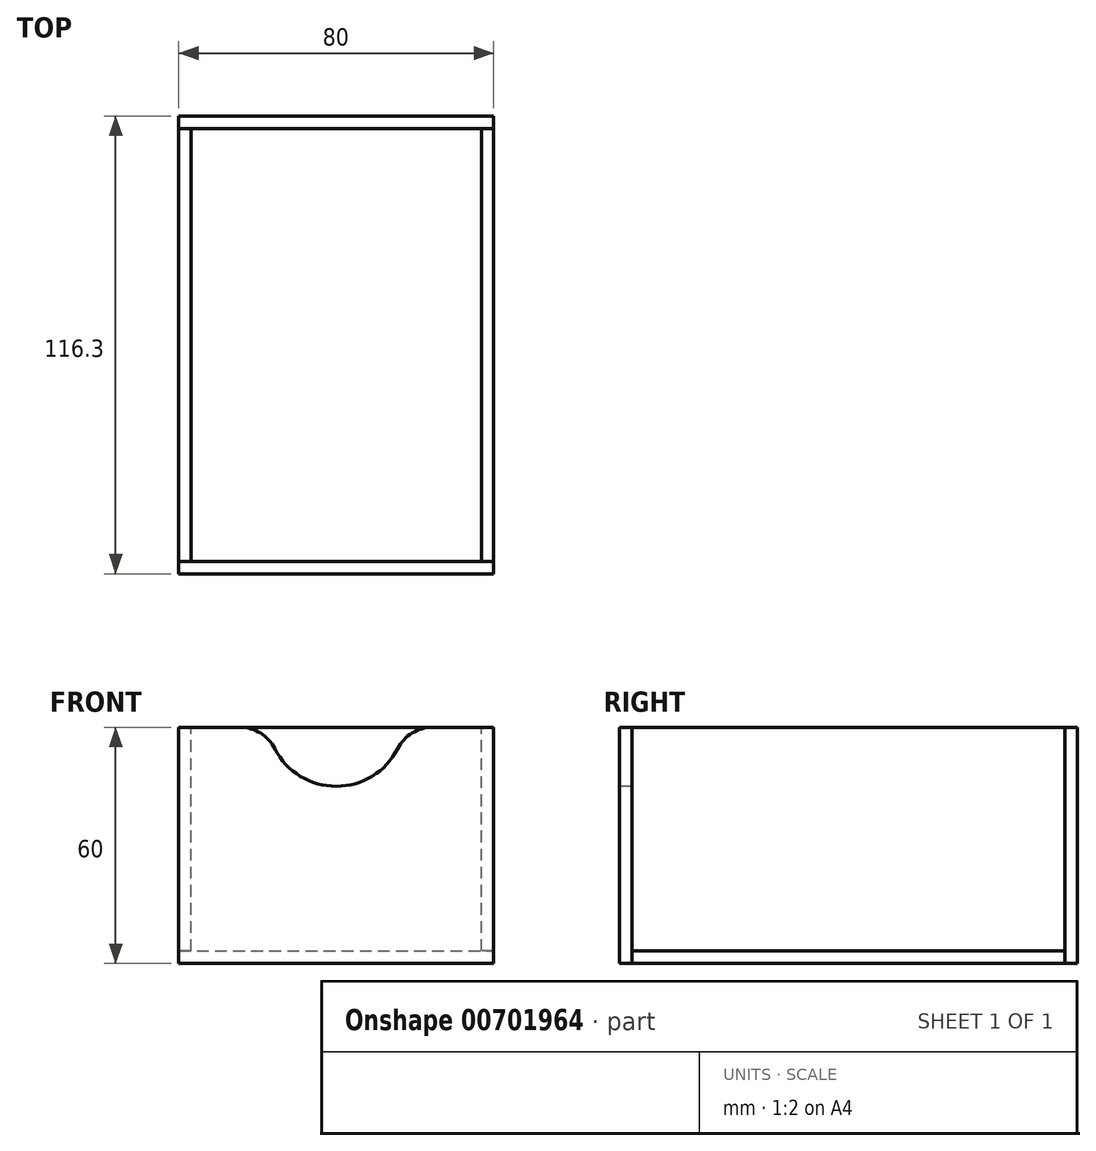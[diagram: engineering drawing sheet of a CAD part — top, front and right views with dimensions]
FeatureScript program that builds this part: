
annotation { "Feature Type Name" : "Feature", "Feature Type Description" : "" }
export const myFeature = defineFeature(function(context is Context, id is Id, definition is map)
    precondition{}
    {
        {
            var Q0;
            Q0=qCreatedBy(makeId("Front.planeOp"),FACE);
            var sketch = newSketch(context, id + "F0", { "sketchPlane" : qUnion([Q0])});
            skLineSegment(sketch, "E0.bottom", {"start": v(0, 0) * mm, "end": v(80, 0) * mm});
            skLineSegment(sketch, "E0.top", {"start": v(0, 60) * mm, "end": v(80, 60) * mm});
            skLineSegment(sketch, "E0.left", {"start": v(0, 0) * mm, "end": v(0, 60) * mm});
            skLineSegment(sketch, "E0.right", {"start": v(80, 0) * mm, "end": v(80, 60) * mm});
            skSolve(sketch);
        }
        {
            var Q0;
            Q0=qSketchRegion(id+"F0",true);
            extrude(context, id + "F1", {"entities" : qUnion([Q0]), "depth" : 3.15 * mm, "offsetDistance" : 25 * mm});
        }
        {
            var Q0;
            Q0=makeQuery(id+"F1.opExtrude","SWEPT_FACE",FACE,{"disambiguationData":[OSD([sQuery(id+"F0.wireOp",EDGE,"E0.bottom")])]});
            var sketch = newSketch(context, id + "F2", { "sketchPlane" : qUnion([Q0])});
            skLineSegment(sketch, "E1.bottom", {"start": v(0, 0) * mm, "end": v(80, 0) * mm});
            skLineSegment(sketch, "E1.top", {"start": v(0, -110) * mm, "end": v(80, -110) * mm});
            skLineSegment(sketch, "E1.left", {"start": v(0, 0) * mm, "end": v(0, -110) * mm});
            skLineSegment(sketch, "E1.right", {"start": v(80, 0) * mm, "end": v(80, -110) * mm});
            skSolve(sketch);
        }
        {
            var Q0;
            Q0=qSketchRegion(id+"F2",true);
            extrude(context, id + "F3", {"entities" : qUnion([Q0]), "oppositeDirection" : true, "depth" : 3.15 * mm, "offsetDistance" : 25 * mm});
        }
        {
            var Q0;
            Q0=makeQuery(id+"F3.opExtrude","SWEPT_FACE",FACE,{"disambiguationData":[OSD([sQuery(id+"F2.wireOp",EDGE,"E1.left")])]});
            var sketch = newSketch(context, id + "F4", { "sketchPlane" : qUnion([Q0])});
            skLineSegment(sketch, "E2.bottom", {"start": v(-110, 3.15) * mm, "end": v(0, 3.15) * mm});
            skLineSegment(sketch, "E2.top", {"start": v(-110, 60) * mm, "end": v(0, 60) * mm});
            skLineSegment(sketch, "E2.left", {"start": v(-110, 3.15) * mm, "end": v(-110, 60) * mm});
            skLineSegment(sketch, "E2.right", {"start": v(0, 3.15) * mm, "end": v(0, 60) * mm});
            skSolve(sketch);
        }
        {
            var Q0;
            Q0=qSketchRegion(id+"F4",true);
            extrude(context, id + "F5", {"entities" : qUnion([Q0]), "oppositeDirection" : true, "depth" : 3.15 * mm, "offsetDistance" : 25 * mm});
        }
        {
            var Q0;
            Q0=makeQuery(id+"F5.opExtrude","SWEPT_BODY",BODY,{"disambiguationData":[OSD([sQuery(id+"F4.wireOp",EDGE,"E2.bottom"),sQuery(id+"F4.wireOp",EDGE,"E2.top"),sQuery(id+"F4.wireOp",EDGE,"E2.left"),sQuery(id+"F4.wireOp",EDGE,"E2.right")])]});
            transform(context, id + "F6", {"entities" : qUnion([Q0]), "transformType" : TransformType.TRANSLATION_3D, "dx" : (81.85 - 5) * mm, "dy" : 0 * mm, "dz" : 0 * mm, "makeCopy" : true});
        }
        {
            var Q0;
            Q0=makeQuery(id+"F3.opExtrude","SWEPT_FACE",FACE,{"disambiguationData":[OSD([sQuery(id+"F2.wireOp",EDGE,"E1.top")])]});
            var sketch = newSketch(context, id + "F7", { "sketchPlane" : qUnion([Q0])});
            skLineSegment(sketch, "E3.bottom", {"start": v(-80, 0) * mm, "end": v(0, 0) * mm});
            skLineSegment(sketch, "E3.top", {"start": v(-80, 60) * mm, "end": v(0, 60) * mm});
            skLineSegment(sketch, "E3.left", {"start": v(-80, 0) * mm, "end": v(-80, 60) * mm});
            skLineSegment(sketch, "E3.right", {"start": v(0, 0) * mm, "end": v(0, 60) * mm});
            skSolve(sketch);
        }
        {
            var Q0;
            Q0=qSketchRegion(id+"F7",true);
            extrude(context, id + "F8", {"entities" : qUnion([Q0]), "depth" : 3.15 * mm, "offsetDistance" : 25 * mm});
        }
        {
            var Q0;
            Q0=makeQuery(id+"F1.opExtrude","CAP_FACE",FACE,{"disambiguationData":[OSD([sQuery(id+"F0.wireOp",EDGE,"E0.bottom"),sQuery(id+"F0.wireOp",EDGE,"E0.top"),sQuery(id+"F0.wireOp",EDGE,"E0.left"),sQuery(id+"F0.wireOp",EDGE,"E0.right")])],"isStart":false});
            var sketch = newSketch(context, id + "F9", { "sketchPlane" : qUnion([Q0])});
            skCircle(sketch, "E4", {"center": v(40, 62.5) * mm, "radius": 17.5 * mm});
            skPoint(sketch, "E4.centerSnap0", {"position": v(40, 60) * mm});
            skLineSegment(sketch, "E5", {"start": v(40, 60) * mm, "end": v(40, 62.5) * mm, "construction": true});
            skSolve(sketch);
        }
        {
            var Q0;
            Q0=qSketchRegion(id+"F9",true);
            extrude(context, id + "F10", {"entities" : qUnion([Q0]), "operationType" : NewBodyOperationType.REMOVE, "oppositeDirection" : true, "depth" : 3.15 * mm, "offsetDistance" : 25 * mm});
        }
        {
            var Q0;
            Q0=makeQuery(id+"F10.boolean.opBoolean","INTERSECT",EDGE,{"disambiguationData":[OD(1.0)],"derivedFrom":[makeQuery(id+"F1.opExtrude","SWEPT_FACE",FACE,{"disambiguationData":[OSD([sQuery(id+"F0.wireOp",EDGE,"E0.top")])]}),makeQuery(id+"F10.opExtrude","SWEPT_FACE",FACE,{"disambiguationData":[OSD([sQuery(id+"F9.wireOp",EDGE,"E4")])]})]});
            var Q1;
            Q1=makeQuery(id+"F10.boolean.opBoolean","INTERSECT",EDGE,{"disambiguationData":[OD(0.0)],"derivedFrom":[makeQuery(id+"F1.opExtrude","SWEPT_FACE",FACE,{"disambiguationData":[OSD([sQuery(id+"F0.wireOp",EDGE,"E0.top")])]}),makeQuery(id+"F10.opExtrude","SWEPT_FACE",FACE,{"disambiguationData":[OSD([sQuery(id+"F9.wireOp",EDGE,"E4")])]})]});
            fillet(context, id + "F11", {"entities" : qUnion([Q0, Q1]), "radius" : 10 * mm, "tangentPropagation" : true, "allowEdgeOverflow" : false});
        }
    });
